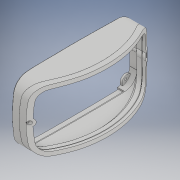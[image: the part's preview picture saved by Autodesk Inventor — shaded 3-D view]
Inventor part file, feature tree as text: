
AUTODESK INVENTOR PART (.ipt)
format: ipt  version: 2019 (Build 230136000, 136)  size: 3,390,464 bytes
history: native  units: mm
features: extrude x14, sketch x10, projected_geometry x6, other x4, hole x3, plane x3, fillet x1
ambient origin geometry x8: Origin, YZ Plane, XZ Plane, XY Plane, X Axis, Y Axis, Z Axis, Center Point
bodies: Volumenkörper3 (feature_tree), Volumenkörper7 (feature_tree), Volumenkörper8 (feature_tree), Volumenkörper9 (feature_tree), Volumenkörper11 (feature_tree)
feature tree (41):
  sketch  "Skizze1"  dims[d8=1.000002mm d10=3.000002mm]
  extrude  "Extrusion3"  Depth=3.000002mm
  extrude  "Extrusion4"  Depth=10.0mm TaperAngle=0.0deg
  sketch  "Skizze2"  dims[d11=1.2mm d12=0.0mm d13=10.0mm d14=0.0mm]
  extrude  "Extrusion5"  Depth=8.0mm
  sketch  "Skizze3"  dims[d16=8.0mm d17=8.0mm]
  hole  "Bohrung1"  [1 undecoded]
  extrude  "Extrusion7"  Depth=138.0mm
  plane  "Arbeitsebene1"
  plane  "Arbeitsebene2"
  extrude  "Extrusion14"  Depth=10.0mm TaperAngle=0.0deg
  sketch  "Skizze7"  dims[d20=3.0mm d21=0.0mm]
  extrude  "Extrusion11"  Depth=140.0mm
  extrude  "Extrusion15"  Depth=3.0mm
  extrude  "Extrusion13"  Depth=6.0mm
  extrude  "Extrusion16"  Depth=40.0mm TaperAngle=0.0deg
  extrude  "Extrusion17"  Depth=3.000001mm
  extrude  "Extrusion20"  Depth=40.0mm TaperAngle=0.0deg
  extrude  "Extrusion21"  Depth=50.0mm TaperAngle=0.0deg
  other  "Kombinieren1"
  extrude  "Extrusion22"  Depth=40.0mm TaperAngle=0.0deg
  other  "Kombinieren2"
  fillet  "Rundung1"  Radius=0.499998mm
  plane  "Arbeitsebene4"
  sketch  "Skizze17"  dims[d49=3.0mm d50=3.0mm]
  hole  "Bohrung3"  [1 undecoded]
  hole  "Bohrung4"  [1 undecoded]
  extrude  "Extrusion25"  Depth=5.0mm
  other  "Kombinieren4"
  other  "Bild1"
  projected_geometry  "Projizierte Kontur1"
  sketch  "Skizze6"  dims[d18=8.0mm d19=8.0mm]
  projected_geometry  "Projizierte Kontur3"
  sketch  "Skizze9"  dims[d26=3.5mm d27=6.0mm d28=4.0mm d29=2.0mm d30=90.0deg d31=8.0mm d32=20.594885mm d33=138.0mm]
  projected_geometry  "Projizierte Kontur4"
  sketch  "Skizze10"  dims[d34=138.0mm d35=10.0mm d36=0.0mm]
  projected_geometry  "Projizierte Kontur5"
  sketch  "Skizze12"  dims[d43=40.0mm d44=0.0mm d45=140.0mm]
  projected_geometry  "Projizierte Kontur7"
  projected_geometry  "Projizierte Kontur10"
  sketch  "Skizze18"  dims[d51=40.0mm d52=0.0mm d53=6.0mm d54=40.0mm d55=0.0mm d56=3.000001mm d57=40.0mm d58=0.0mm d59=50.0mm d60=0.0mm d61=40.0mm d62=0.0mm d63=0.499998mm d69=50.0mm d70=0.0mm d71=40.0mm d72=0.0mm d73=5.0mm d74=40.0mm d75=0.0mm d76=0.75mm d77=3.0mm d95=50.0mm d96=6.0mm d97=6.0mm d98=3.0mm d99=6.0mm d100=4.0mm d101=2.0mm d102=90.0deg d103=8.0mm d104=20.594885mm d105=5.5mm d106=6.0mm d107=4.0mm d108=2.0mm d109=90.0deg d110=30.0mm d111=0.0mm d112=40.0mm d113=0.0mm]
note: 3 required parameter values undecoded (feature->parameter linkage not recoverable at this tier; creation-order binding heuristic only, values carry confidence <= 0.55)
